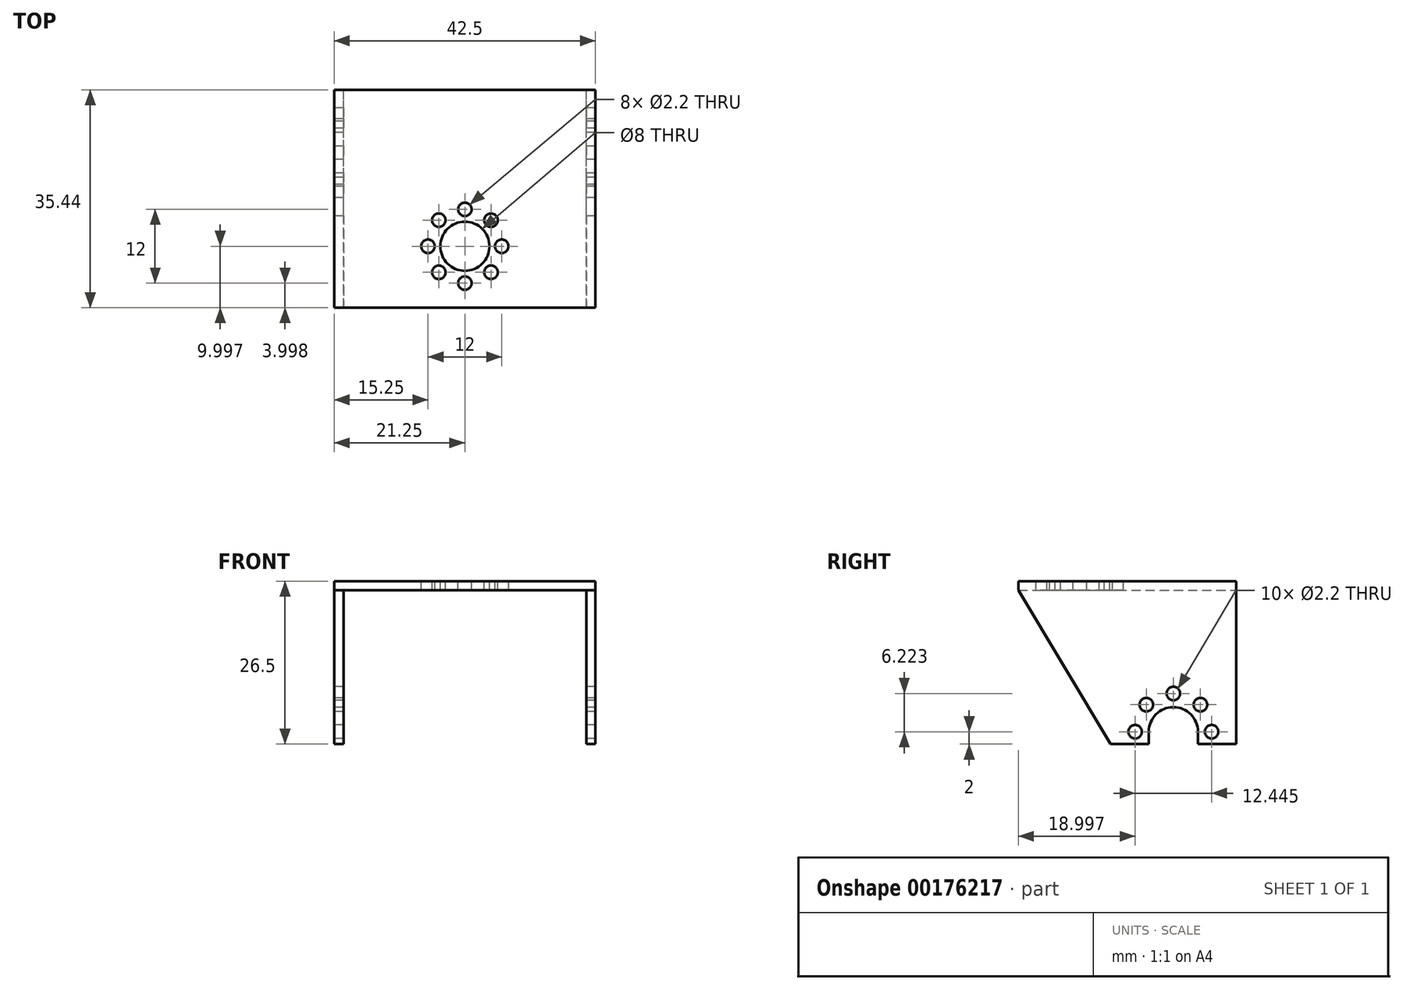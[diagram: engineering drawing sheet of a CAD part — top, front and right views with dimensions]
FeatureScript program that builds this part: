
annotation { "Feature Type Name" : "Feature", "Feature Type Description" : "" }
export const myFeature = defineFeature(function(context is Context, id is Id, definition is map)
    precondition{}
    {
        {
            var Q0;
            Q0=qCreatedBy(makeId("Front.planeOp"),FACE);
            var sketch = newSketch(context, id + "F0", { "sketchPlane" : qUnion([Q0])});
            skLineSegment(sketch, "E0.bottom", {"start": v(0, 0) * mm, "end": v(1.5, 0) * mm});
            skLineSegment(sketch, "E0.top", {"start": v(0, 26.5) * mm, "end": v(42.5, 26.5) * mm});
            skLineSegment(sketch, "E0.left", {"start": v(0, 0) * mm, "end": v(0, 26.5) * mm});
            skLineSegment(sketch, "E0.right", {"start": v(42.5, 0) * mm, "end": v(42.5, 26.5) * mm});
            skLineSegment(sketch, "E1.top", {"start": v(1.5, 25) * mm, "end": v(41, 25) * mm});
            skLineSegment(sketch, "E1.left", {"start": v(1.5, 0) * mm, "end": v(1.5, 25) * mm});
            skLineSegment(sketch, "E1.right", {"start": v(41, 0) * mm, "end": v(41, 25) * mm});
            skLineSegment(sketch, "E2.trimOffspring", {"start": v(41, 0) * mm, "end": v(42.5, 0) * mm});
            skSolve(sketch);
        }
        {
            var Q0;
            Q0=qSketchRegion(id+"F0",true);
            extrude(context, id + "F1", {"entities" : qUnion([Q0]), "depth" : 33 * mm});
        }
        {
            var Q0;
            Q0=makeQuery(id+"F1.opExtrude","SWEPT_FACE",FACE,{"disambiguationData":[OSD([sQuery(id+"F0.wireOp",EDGE,"E0.left")])]});
            var sketch = newSketch(context, id + "F2", { "sketchPlane" : qUnion([Q0])});
            skArc(sketch, "E3", {"start": v(20.5, 2) * mm, "mid": v(16.5, 6) * mm, "end": v(12.5, 2) * mm});
            skCircle(sketch, "E4", {"center": v(22.72, 2) * mm, "radius": 1.1 * mm});
            skCircle(sketch, "E5.1.0", {"center": v(20.9, 6.4) * mm, "radius": 1.1 * mm});
            skCircle(sketch, "E5.2.0", {"center": v(16.5, 8.22) * mm, "radius": 1.1 * mm});
            skCircle(sketch, "E5.3.0", {"center": v(12.1, 6.4) * mm, "radius": 1.1 * mm});
            skCircle(sketch, "E5.4.0", {"center": v(10.28, 2) * mm, "radius": 1.1 * mm});
            skLineSegment(sketch, "E6", {"start": v(12.5, 2) * mm, "end": v(12.5, 0) * mm});
            skLineSegment(sketch, "E7", {"start": v(20.5, 2) * mm, "end": v(20.5, 0) * mm});
            skLineSegment(sketch, "E8", {"start": v(12.5, 0) * mm, "end": v(20.5, 0) * mm});
            skLineSegment(sketch, "E9", {"start": v(16.5, 26.5) * mm, "end": v(16.5, 0) * mm, "construction": true});
            skPoint(sketch, "E10", {"position": v(16.5, 0) * mm});
            skLineSegment(sketch, "E11", {"start": v(6.28, 0) * mm, "end": v(0, 25) * mm});
            skLineSegment(sketch, "E12", {"start": v(6.28, 0) * mm, "end": v(0, 0) * mm});
            skLineSegment(sketch, "E13", {"start": v(0, 0) * mm, "end": v(0, 25) * mm});
            skLineSegment(sketch, "E14.MirrorCS", {"start": v(33, 0) * mm, "end": v(33, 25) * mm});
            skLineSegment(sketch, "E15.MirrorCS", {"start": v(26.72, 0) * mm, "end": v(33, 25) * mm});
            skLineSegment(sketch, "E16.MirrorCS", {"start": v(26.72, 0) * mm, "end": v(33, 0) * mm});
            skLineSegment(sketch, "E17.bottom", {"start": v(33, 0) * mm, "end": v(26.72, 0) * mm});
            skLineSegment(sketch, "E17.top", {"start": v(33, 25) * mm, "end": v(26.72, 25) * mm});
            skLineSegment(sketch, "E17.right", {"start": v(26.72, 0) * mm, "end": v(26.72, 25) * mm});
            skLineSegment(sketch, "E18.MirrorCS", {"start": v(0, 25) * mm, "end": v(6.28, 25) * mm});
            skLineSegment(sketch, "E19.MirrorCS", {"start": v(6.28, 0) * mm, "end": v(6.28, 25) * mm});
            skLineSegment(sketch, "E20.bottom", {"start": v(33, 26.5) * mm, "end": v(26.72, 26.5) * mm});
            skLineSegment(sketch, "E20.left", {"start": v(33, 26.5) * mm, "end": v(33, 25) * mm});
            skLineSegment(sketch, "E20.right", {"start": v(26.72, 26.5) * mm, "end": v(26.72, 25) * mm});
            skLineSegment(sketch, "E21.top", {"start": v(0, 26.5) * mm, "end": v(6.28, 26.5) * mm});
            skLineSegment(sketch, "E21.left", {"start": v(0, 25) * mm, "end": v(0, 26.5) * mm});
            skLineSegment(sketch, "E21.right", {"start": v(6.28, 25) * mm, "end": v(6.28, 26.5) * mm});
            skSolve(sketch);
        }
        {
            var Q0;
            Q0=qSketchRegion(id+"F2",true);
            extrude(context, id + "F3", {"entities" : qUnion([Q0]), "operationType" : NewBodyOperationType.REMOVE, "endBound" : BoundingType.THROUGH_ALL, "oppositeDirection" : true, "depth" : 25 * mm});
        }
        {
            var Q0;
            Q0=makeQuery(id+"F3.boolean.opBoolean","COPY",FACE,{"derivedFrom":makeQuery(id+"F3.opExtrude","SWEPT_FACE",FACE,{"disambiguationData":[OSD([sQuery(id+"F2.wireOp",EDGE,"E17.right"),sQuery(id+"F2.wireOp",EDGE,"E20.right")])]})});
            var sketch = newSketch(context, id + "F4", { "sketchPlane" : qUnion([Q0])});
            skLineSegment(sketch, "E22.0", {"start": v(1.5, 25) * mm, "end": v(1.5, 0) * mm});
            skLineSegment(sketch, "E23.0", {"start": v(0, 26.5) * mm, "end": v(0, 0) * mm});
            skLineSegment(sketch, "E24.0", {"start": v(42.5, 26.5) * mm, "end": v(0, 26.5) * mm});
            skLineSegment(sketch, "E25.0", {"start": v(42.5, 26.5) * mm, "end": v(42.5, 0) * mm});
            skLineSegment(sketch, "E26.0", {"start": v(41, 25) * mm, "end": v(1.5, 25) * mm});
            skLineSegment(sketch, "E27.0", {"start": v(41, 25) * mm, "end": v(41, 0) * mm});
            skLineSegment(sketch, "E28.0", {"start": v(1.5, 0) * mm, "end": v(0, 0) * mm});
            skLineSegment(sketch, "E29.0", {"start": v(42.5, 0) * mm, "end": v(41, 0) * mm});
            skSolve(sketch);
        }
        {
            var Q0;
            Q0=qSketchRegion(id+"F4",true);
            extrude(context, id + "F5", {"entities" : qUnion([Q0]), "operationType" : NewBodyOperationType.ADD, "depth" : 15 * mm});
        }
        {
            var Q0;
            Q0=makeQuery(id+"F5.boolean.opBoolean","MERGE",FACE,{"derivedFrom":[makeQuery(id+"F1.opExtrude","SWEPT_FACE",FACE,{"disambiguationData":[OSD([sQuery(id+"F0.wireOp",EDGE,"E0.right")])]}),makeQuery(id+"F5.opExtrude","SWEPT_FACE",FACE,{"disambiguationData":[OSD([sQuery(id+"F4.wireOp",EDGE,"E25.0")])]})]});
            var sketch = newSketch(context, id + "F6", { "sketchPlane" : qUnion([Q0])});
            skLineSegment(sketch, "E30", {"start": v(-41.72, 25) * mm, "end": v(-26.72, 0) * mm});
            skPoint(sketch, "E31", {"position": v(-22.72, 2) * mm});
            skPoint(sketch, "E32", {"position": v(-10.28, 2) * mm});
            skSolve(sketch);
        }
        {
            var Q0;
            Q0=qSketchRegion(id+"F6",true);
            var Q1;
            {var subQ0=sQuery(id+"F6.wireOp",EDGE,"E30");Q1=makeQuery(id+"F6.imprint","IMPRINT",FACE,{"disambiguationData":[TD([[makeQuery(id+"F6.imprint","IMPRINT",EDGE,{"derivedFrom":subQ0}),-1.0]])]});}
            extrude(context, id + "F7", {"entities" : qUnion([Q0, Q1]), "operationType" : NewBodyOperationType.REMOVE, "endBound" : BoundingType.THROUGH_ALL, "oppositeDirection" : true, "depth" : 25 * mm});
        }
        {
            var Q0;
            Q0=makeQuery(id+"F5.boolean.opBoolean","MERGE",FACE,{"derivedFrom":[makeQuery(id+"F1.opExtrude","SWEPT_FACE",FACE,{"disambiguationData":[OSD([sQuery(id+"F0.wireOp",EDGE,"E0.top")])]}),makeQuery(id+"F5.opExtrude","SWEPT_FACE",FACE,{"disambiguationData":[OSD([sQuery(id+"F4.wireOp",EDGE,"E24.0")])]})]});
            var sketch = newSketch(context, id + "F8", { "sketchPlane" : qUnion([Q0])});
            skLineSegment(sketch, "E33", {"start": v(21.25, -6.28) * mm, "end": v(21.25, -41.72) * mm, "construction": true});
            skCircle(sketch, "E34", {"center": v(21.25, -31.72) * mm, "radius": 4 * mm});
            skCircle(sketch, "E35", {"center": v(21.25, -37.72) * mm, "radius": 1.1 * mm});
            skCircle(sketch, "E36.1.0", {"center": v(25.5, -35.97) * mm, "radius": 1.1 * mm});
            skCircle(sketch, "E36.2.0", {"center": v(27.25, -31.72) * mm, "radius": 1.1 * mm});
            skCircle(sketch, "E36.3.0", {"center": v(25.5, -27.48) * mm, "radius": 1.1 * mm});
            skCircle(sketch, "E36.4.0", {"center": v(21.25, -25.72) * mm, "radius": 1.1 * mm});
            skCircle(sketch, "E36.5.0", {"center": v(17, -27.48) * mm, "radius": 1.1 * mm});
            skCircle(sketch, "E36.6.0", {"center": v(15.25, -31.72) * mm, "radius": 1.1 * mm});
            skCircle(sketch, "E36.7.0", {"center": v(17, -35.97) * mm, "radius": 1.1 * mm});
            skSolve(sketch);
        }
        {
            var Q0;
            Q0=qSketchRegion(id+"F8",true);
            extrude(context, id + "F9", {"entities" : qUnion([Q0]), "operationType" : NewBodyOperationType.REMOVE, "endBound" : BoundingType.UP_TO_NEXT, "oppositeDirection" : true, "depth" : 25 * mm});
        }
    });
